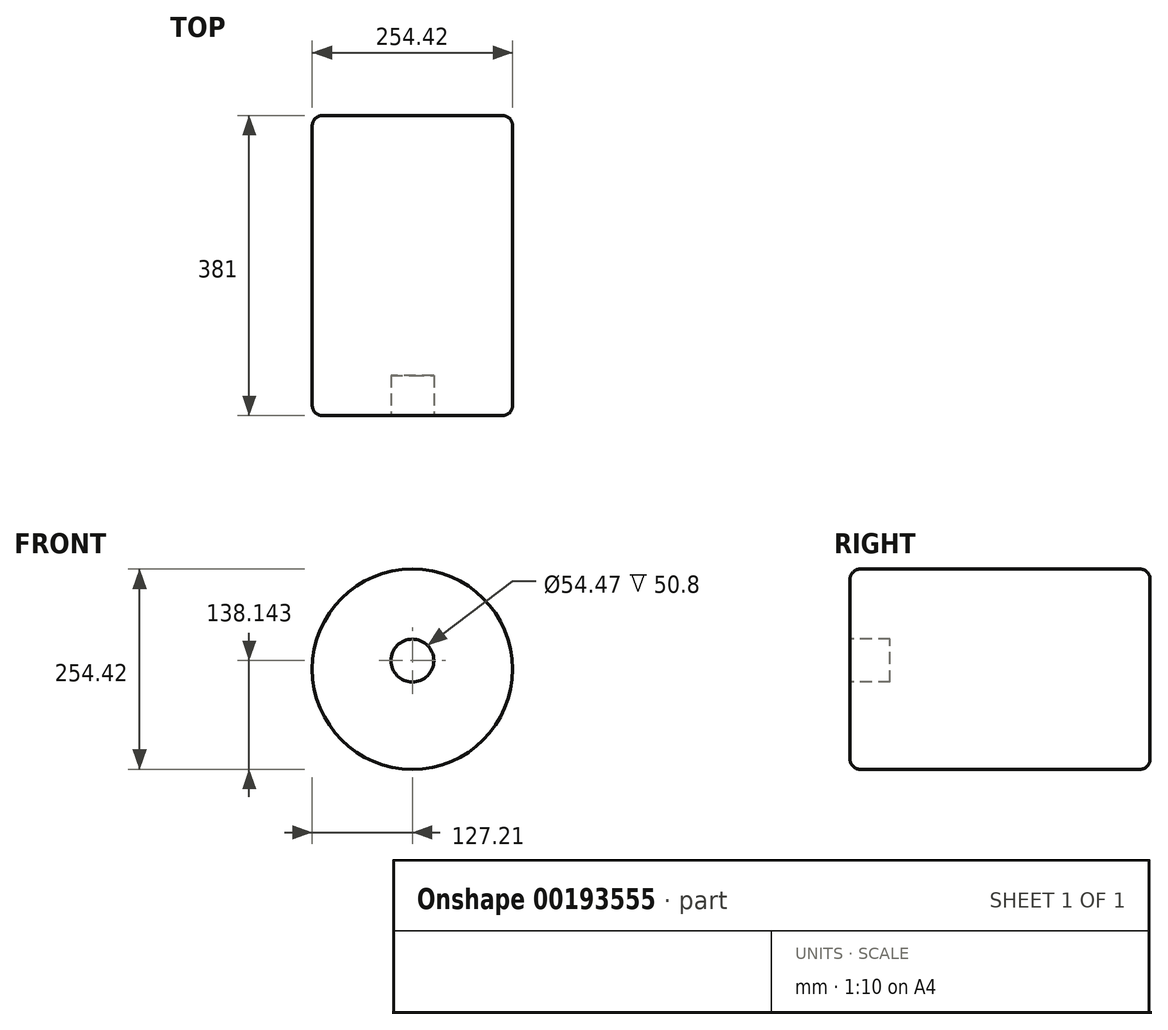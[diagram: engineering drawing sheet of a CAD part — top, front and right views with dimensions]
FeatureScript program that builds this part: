
annotation { "Feature Type Name" : "Feature", "Feature Type Description" : "" }
export const myFeature = defineFeature(function(context is Context, id is Id, definition is map)
    precondition{}
    {
        {
            var Q0;
            Q0=qCreatedBy(makeId("Front.planeOp"),FACE);
            var sketch = newSketch(context, id + "F0", { "sketchPlane" : qUnion([Q0])});
            skCircle(sketch, "E0", {"center": v(0, 0) * mm, "radius": 127.2 * mm});
            skSolve(sketch);
        }
        {
            var Q0;
            Q0=makeQuery(id+"F0.imprint","IMPRINT",FACE,{"disambiguationData":[TD([[makeQuery(id+"F0.imprint","IMPRINT",EDGE,{"derivedFrom":sQuery(id+"F0.wireOp",EDGE,"E0")}),1.0]])]});
            extrude(context, id + "F1", {"entities" : qUnion([Q0]), "depth" : 381 * mm});
        }
        {
            var Q0;
            Q0=makeQuery(id+"F1.opExtrude","CAP_FACE",FACE,{"disambiguationData":[OSD([sQuery(id+"F0.wireOp",EDGE,"E0")])],"isStart":false});
            var sketch = newSketch(context, id + "F2", { "sketchPlane" : qUnion([Q0])});
            skCircle(sketch, "E1", {"center": v(0, 10.93) * mm, "radius": 27.24 * mm});
            skSolve(sketch);
        }
        {
            var Q0;
            Q0=makeQuery(id+"F2.imprint","IMPRINT",FACE,{"disambiguationData":[TD([[makeQuery(id+"F2.imprint","IMPRINT",EDGE,{"derivedFrom":sQuery(id+"F2.wireOp",EDGE,"E1")}),1.0]])]});
            extrude(context, id + "F3", {"entities" : qUnion([Q0]), "operationType" : NewBodyOperationType.REMOVE, "oppositeDirection" : true, "depth" : 50.8 * mm});
        }
        {
            var Q0;
            Q0=makeQuery(id+"F1.opExtrude","CAP_EDGE",EDGE,{"disambiguationData":[OSD([sQuery(id+"F0.wireOp",EDGE,"E0")])],"isStart":false});
            fillet(context, id + "F4", {"entities" : qUnion([Q0]), "radius" : 12.7 * mm, "tangentPropagation" : true, "allowEdgeOverflow" : false});
        }
        {
            var Q0;
            Q0=makeQuery(id+"F1.opExtrude","CAP_EDGE",EDGE,{"disambiguationData":[OSD([sQuery(id+"F0.wireOp",EDGE,"E0")])],"isStart":true});
            fillet(context, id + "F5", {"entities" : qUnion([Q0]), "radius" : 12.7 * mm, "tangentPropagation" : true, "allowEdgeOverflow" : false});
        }
    });
